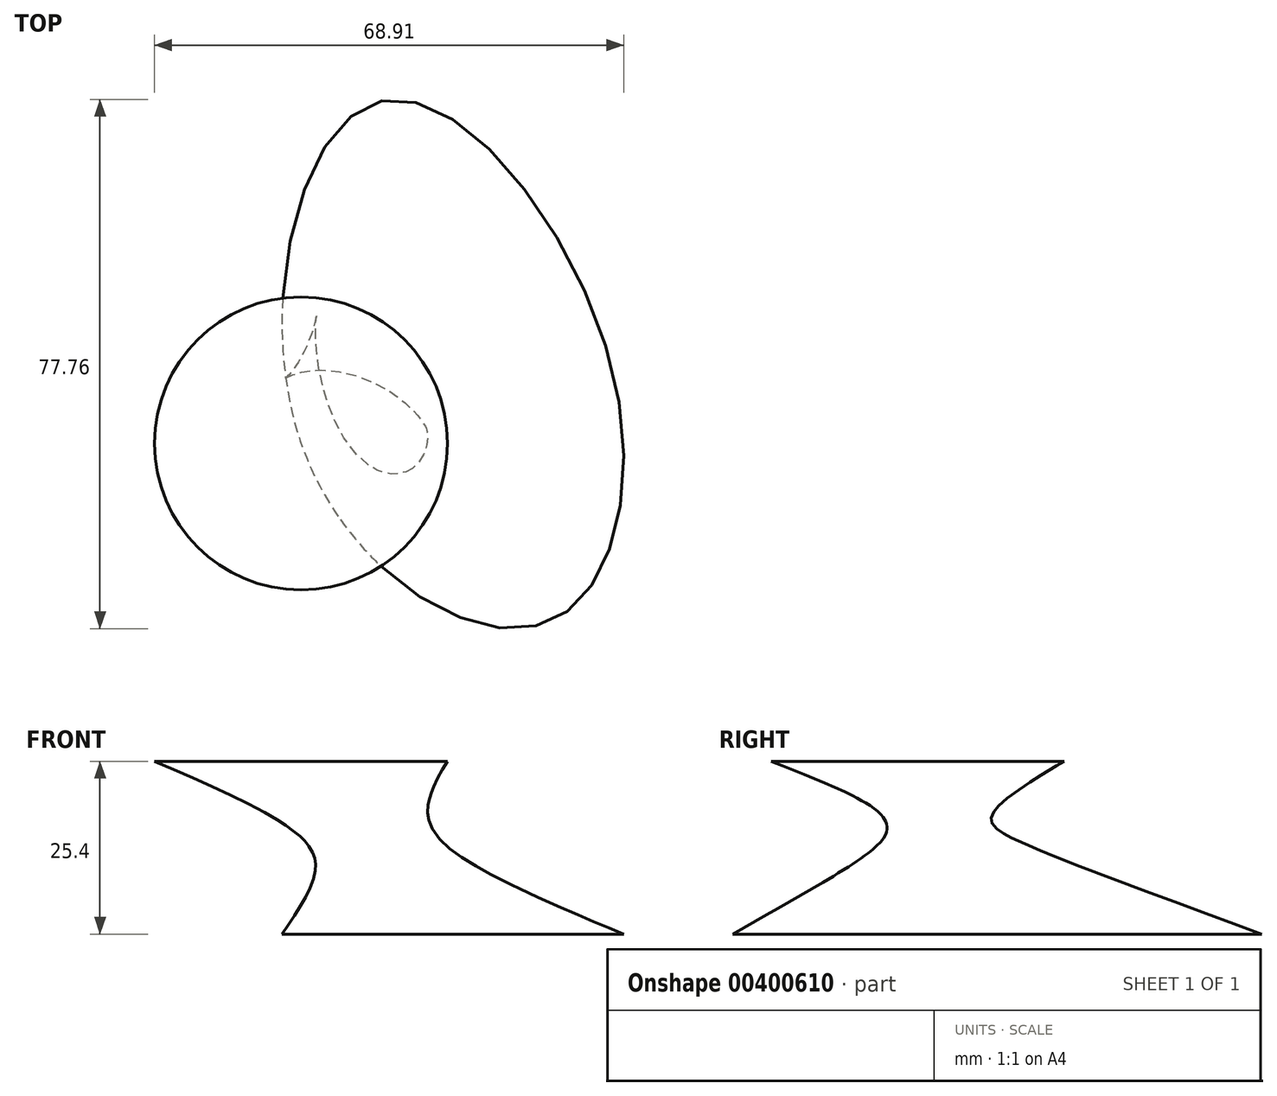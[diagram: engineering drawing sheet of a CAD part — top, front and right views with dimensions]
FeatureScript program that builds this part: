
annotation { "Feature Type Name" : "Feature", "Feature Type Description" : "" }
export const myFeature = defineFeature(function(context is Context, id is Id, definition is map)
    precondition{}
    {
        {
            var Q0;
            Q0=qCreatedBy(makeId("Top.planeOp"),FACE);
            cPlane(context, id + "F0", {"entities" : qUnion([Q0]), "cplaneType" : CPlaneType.OFFSET, "offset" : 25.4 * mm, "width" : 152.4 * mm, "height" : 152.4 * mm});
        }
        {
            var Q0;
            Q0=qCreatedBy(id+"F0.planeOp",FACE);
            var sketch = newSketch(context, id + "F1", { "sketchPlane" : qUnion([Q0])});
            skCircle(sketch, "E0", {"center": v(0, 0) * mm, "radius": 21.52 * mm});
            skSolve(sketch);
        }
        {
            var Q0;
            Q0=qCreatedBy(makeId("Top.planeOp"),FACE);
            var sketch = newSketch(context, id + "F2", { "sketchPlane" : qUnion([Q0])});
            skFitSpline(sketch, "E1", {"points": [v(0, 0) * mm, v(35.38, -26.58) * mm, v(45.56, 11.5) * mm, v(11.48, 50.26) * mm, v(0, 0) * mm]});
            skSolve(sketch);
        }
        {
            var Q0;
            Q0 = qSketchRegion(id + "F1", true);
            var Q1;
            Q1 = qSketchRegion(id + "F2", true);
            loft(context, id + "F3", {"sheetProfilesArray" : [{ "sheetProfileEntities" : qUnion([Q0]) }, { "sheetProfileEntities" : qUnion([Q1]) }]});
        }
    });
